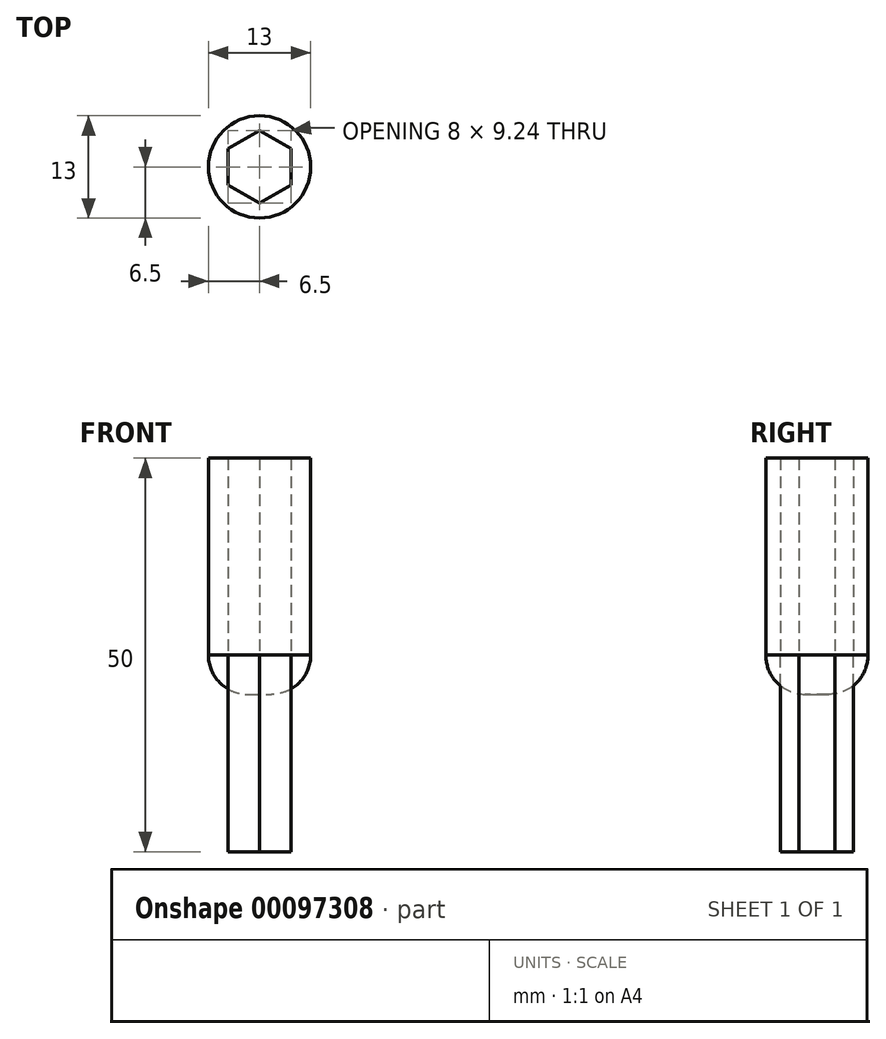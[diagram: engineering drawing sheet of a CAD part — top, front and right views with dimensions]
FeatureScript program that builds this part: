
annotation { "Feature Type Name" : "Feature", "Feature Type Description" : "" }
export const myFeature = defineFeature(function(context is Context, id is Id, definition is map)
    precondition{}
    {
        {
            var Q0;
            Q0=qCreatedBy(makeId("Top.planeOp"),FACE);
            var sketch = newSketch(context, id + "F0", { "sketchPlane" : qUnion([Q0])});
            skCircle(sketch, "E0.cCircle", {"center": v(0, 0) * mm, "radius": 4 * mm, "construction": true});
            skLineSegment(sketch, "E0.0", {"start": v(4, 2.3) * mm, "end": v(4, -2.3) * mm});
            skLineSegment(sketch, "E0.1", {"start": v(4, -2.3) * mm, "end": v(0, -4.62) * mm});
            skLineSegment(sketch, "E0.2", {"start": v(0, -4.62) * mm, "end": v(-4, -2.3) * mm});
            skLineSegment(sketch, "E0.3", {"start": v(-4, -2.3) * mm, "end": v(-4, 2.3) * mm});
            skLineSegment(sketch, "E0.4", {"start": v(-4, 2.3) * mm, "end": v(0, 4.62) * mm});
            skLineSegment(sketch, "E0.5", {"start": v(0, 4.62) * mm, "end": v(4, 2.3) * mm});
            skPoint(sketch, "E0.0.midPoint", {"position": v(4, 0) * mm});
            skCircle(sketch, "E1", {"center": v(0, 0) * mm, "radius": 6.5 * mm});
            skSolve(sketch);
        }
        {
            var Q0;
            Q0=makeQuery(id+"F0.imprint","IMPRINT",FACE,{"disambiguationData":[TD([[makeQuery(id+"F0.imprint","IMPRINT",EDGE,{"derivedFrom":sQuery(id+"F0.wireOp",EDGE,"E0.0")}),1.0]])]});
            var Q1;
            Q1=sQuery(id+"F0.wireOp",EDGE,"E1");
            extrude(context, id + "F1", {"entities" : qUnion([Q0]), "surfaceEntities" : qUnion([Q1]), "depth" : 25 * mm});
        }
        {
            var Q0;
            Q0=makeQuery(id+"F1.opExtrude","CAP_FACE",FACE,{"disambiguationData":[OSD([sQuery(id+"F0.wireOp",EDGE,"E0.0"),sQuery(id+"F0.wireOp",EDGE,"E0.1"),sQuery(id+"F0.wireOp",EDGE,"E0.2"),sQuery(id+"F0.wireOp",EDGE,"E0.3"),sQuery(id+"F0.wireOp",EDGE,"E0.4"),sQuery(id+"F0.wireOp",EDGE,"E0.5"),sQuery(id+"F0.wireOp",EDGE,"E1")])],"isStart":true});
            var sketch = newSketch(context, id + "F2", { "sketchPlane" : qUnion([Q0])});
            skCircle(sketch, "E2.cCircle", {"center": v(0, 0) * mm, "radius": 4 * mm, "construction": true});
            skLineSegment(sketch, "E2.0", {"start": v(-4, -2.3) * mm, "end": v(-4, 2.3) * mm});
            skLineSegment(sketch, "E2.1", {"start": v(-4, 2.3) * mm, "end": v(0, 4.62) * mm});
            skLineSegment(sketch, "E2.2", {"start": v(0, 4.62) * mm, "end": v(4, 2.3) * mm});
            skLineSegment(sketch, "E2.3", {"start": v(4, 2.3) * mm, "end": v(4, -2.3) * mm});
            skLineSegment(sketch, "E2.4", {"start": v(4, -2.3) * mm, "end": v(0, -4.62) * mm});
            skLineSegment(sketch, "E2.5", {"start": v(0, -4.62) * mm, "end": v(-4, -2.3) * mm});
            skPoint(sketch, "E2.0.midPoint", {"position": v(-4, 0) * mm});
            skSolve(sketch);
        }
        {
            var Q0;
            Q0=makeQuery(id+"F2.imprint","IMPRINT",FACE,{"disambiguationData":[TD([[makeQuery(id+"F2.imprint","IMPRINT",EDGE,{"derivedFrom":sQuery(id+"F2.wireOp",EDGE,"E2.0")}),1.0]])]});
            extrude(context, id + "F3", {"entities" : qUnion([Q0]), "depth" : 25 * mm});
        }
        {
            var Q0;
            Q0=makeQuery(id+"F1.opExtrude","CAP_FACE",FACE,{"disambiguationData":[OSD([sQuery(id+"F0.wireOp",EDGE,"E0.0"),sQuery(id+"F0.wireOp",EDGE,"E0.1"),sQuery(id+"F0.wireOp",EDGE,"E0.2"),sQuery(id+"F0.wireOp",EDGE,"E0.3"),sQuery(id+"F0.wireOp",EDGE,"E0.4"),sQuery(id+"F0.wireOp",EDGE,"E0.5"),sQuery(id+"F0.wireOp",EDGE,"E1")])],"isStart":true});
            var sketch = newSketch(context, id + "F4", { "sketchPlane" : qUnion([Q0])});
            skCircle(sketch, "E3", {"center": v(0, 0) * mm, "radius": 6.5 * mm});
            skSolve(sketch);
        }
        {
            var Q0;
            Q0 = qSketchRegion(id + "F4", true);
            extrude(context, id + "F5", {"entities" : qUnion([Q0]), "depth" : 5 * mm});
        }
        {
            var Q0;
            Q0=makeQuery(id+"F5.opExtrude","CAP_FACE",FACE,{"disambiguationData":[OSD([sQuery(id+"F4.wireOp",EDGE,"E3")])],"isStart":false});
            fillet(context, id + "F6", {"entities" : qUnion([Q0]), "radius" : 5 * mm, "tangentPropagation" : true, "allowEdgeOverflow" : false});
        }
    });
